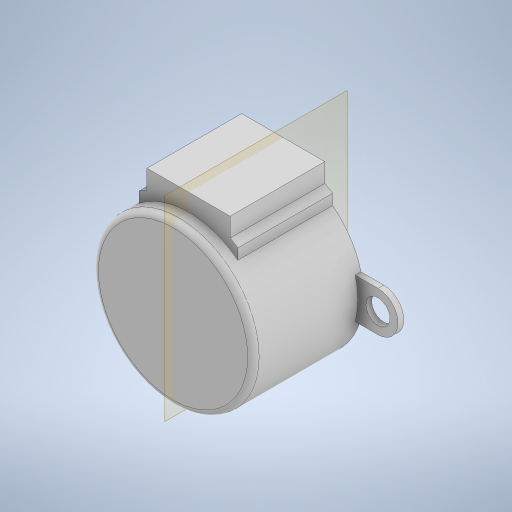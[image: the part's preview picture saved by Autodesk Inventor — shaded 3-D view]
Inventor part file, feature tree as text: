
AUTODESK INVENTOR PART (.ipt)
format: ipt  version: 2023 (Build 270158000, 158)  size: 383,488 bytes
history: native  units: mm
features: extrude x6, sketch x6, other x1, fillet x1
ambient origin geometry x8: Origin, YZ Plane, XZ Plane, XY Plane, X Axis, Y Axis, Z Axis, Center Point
bodies: Body1 (feature_tree)
feature tree (14):
  other  "Těleso1"
  extrude  "Vysunutí1"  Depth=19.2mm TaperAngle=0.0deg
  fillet  "Zaoblení1"  Radius=1.0mm
  extrude  "Vysunutí2"  Depth=14.5mm
  extrude  "Vysunutí3"  Depth=1.0mm
  extrude  "Vysunutí4"  Depth=17.2mm
  extrude  "Vysunutí5"  Depth=1.35mm
  extrude  "Extrusion6"  Depth=1.35mm
  sketch  "Náčrt1"
  sketch  "Náčrt2"
  sketch  "Náčrt3"
  sketch  "Náčrt4"
  sketch  "Náčrt5"
  sketch  "Sketch6"  dims[d0=28.0mm d1=19.2mm d2=0.0mm d3=1.0mm d4=14.5mm d5=31.0mm d6=17.2mm d7=1.35mm d8=1.35mm d9=1.5mm d10=16.5mm d11=0.0mm d12=9.2mm d14=1.4mm d15=1.7mm d16=0.0mm d17=5.0mm d18=2.95mm d19=8.0mm d20=0.0mm d21=2.0mm d22=0.0mm d23=4.2mm d24=35.0mm d25=7.0mm d26=1.0mm d27=0.0mm]
